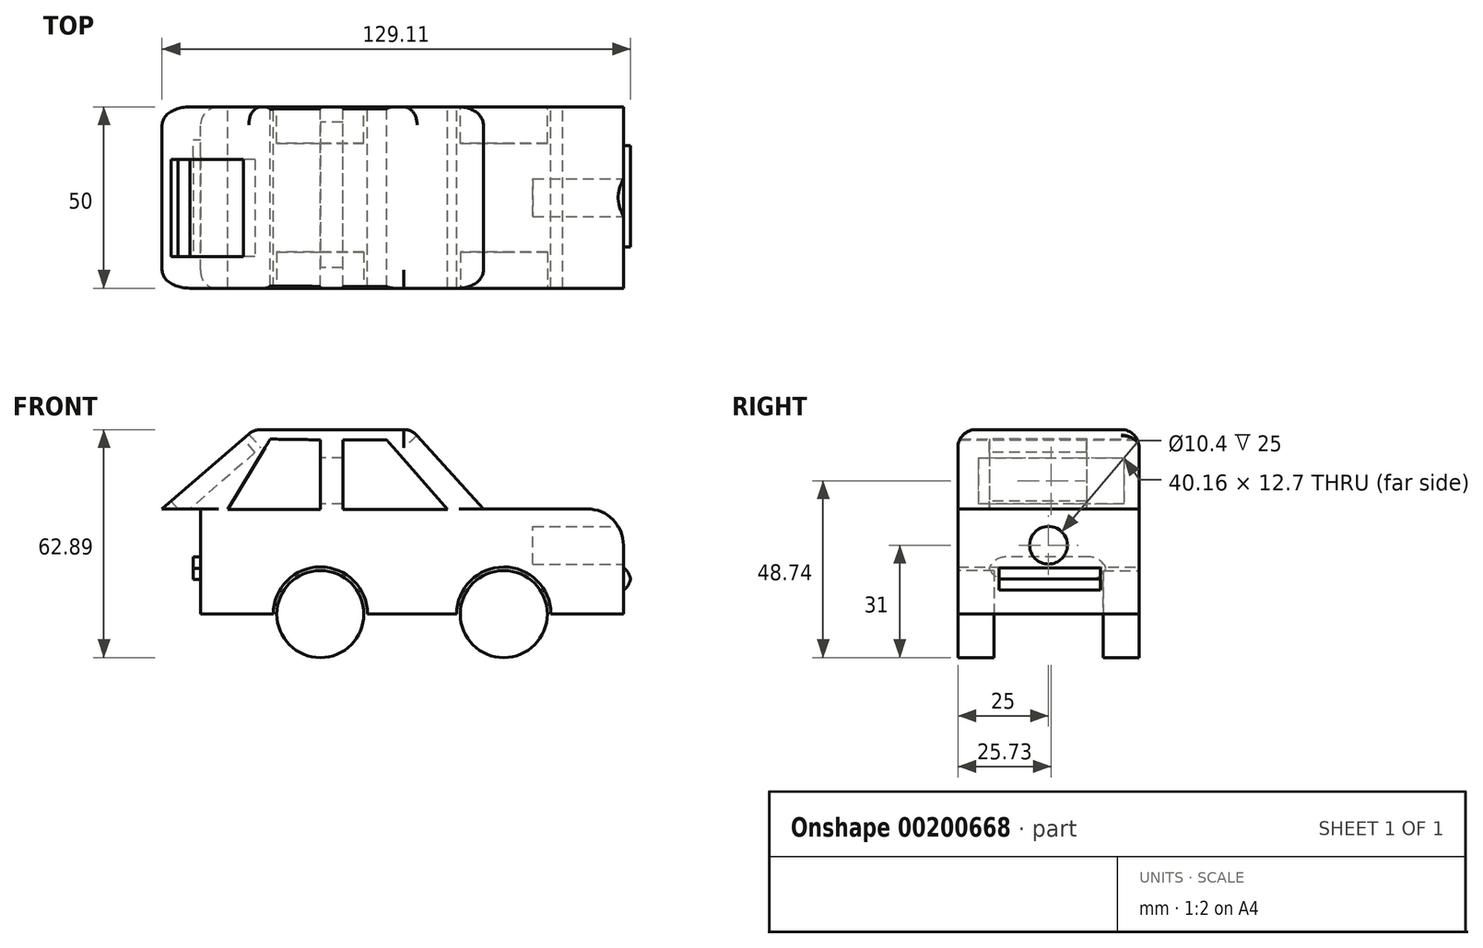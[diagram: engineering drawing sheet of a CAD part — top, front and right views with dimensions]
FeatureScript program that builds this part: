
annotation { "Feature Type Name" : "Feature", "Feature Type Description" : "" }
export const myFeature = defineFeature(function(context is Context, id is Id, definition is map)
    precondition{}
    {
        {
            var Q0;
            Q0=qCreatedBy(makeId("Front.planeOp"),FACE);
            var sketch = newSketch(context, id + "F0", { "sketchPlane" : qUnion([Q0])});
            skLineSegment(sketch, "E0", {"start": v(-31.77, -12.79) * mm, "end": v(-13, -12.79) * mm});
            skLineSegment(sketch, "E1", {"start": v(13, -12.79) * mm, "end": v(37.3, -12.79) * mm});
            skLineSegment(sketch, "E2", {"start": v(66.84, -12.79) * mm, "end": v(83.56, -12.79) * mm});
            skLineSegment(sketch, "E3", {"start": v(83.56, -12.79) * mm, "end": v(83.56, 16.21) * mm});
            skLineSegment(sketch, "E4", {"start": v(83.56, 16.21) * mm, "end": v(44.95, 16.21) * mm});
            skLineSegment(sketch, "E5", {"start": v(44.95, 16.21) * mm, "end": v(25.18, 38.1) * mm});
            skLineSegment(sketch, "E6", {"start": v(25.18, 38.1) * mm, "end": v(-18.32, 38.1) * mm});
            skLineSegment(sketch, "E7", {"start": v(-18.32, 38.1) * mm, "end": v(-43.63, 16.21) * mm});
            skLineSegment(sketch, "E8", {"start": v(-33, 16.21) * mm, "end": v(-43.63, 16.21) * mm});
            skLineSegment(sketch, "E9", {"start": v(-33, 16.21) * mm, "end": v(-33, -10.15) * mm});
            skLineSegment(sketch, "E10", {"start": v(-33, -10.15) * mm, "end": v(-33, -12.79) * mm});
            skLineSegment(sketch, "E11", {"start": v(-33, -12.79) * mm, "end": v(-31.77, -12.79) * mm});
            skArc(sketch, "E12", {"start": v(13, -12.79) * mm, "mid": v(0, 0.21) * mm, "end": v(-13, -12.79) * mm});
            skArc(sketch, "E13", {"start": v(63.56, -12.7) * mm, "mid": v(50.52, 0.21) * mm, "end": v(37.56, -12.79) * mm});
            skPoint(sketch, "E13.centerSnap0", {"position": v(7.3, -12.79) * mm});
            skLineSegment(sketch, "E14", {"start": v(63.56, -12.7) * mm, "end": v(66.84, -12.79) * mm});
            skLineSegment(sketch, "E15", {"start": v(37.3, -12.79) * mm, "end": v(37.56, -12.79) * mm});
            skPoint(sketch, "E16.trimOffspring.end.orphan", {"position": v(-22.7, -12.79) * mm});
            skSolve(sketch);
        }
        {
            var Q0;
            Q0=makeQuery(id+"F0.imprint","IMPRINT",FACE,{"disambiguationData":[TD([[makeQuery(id+"F0.imprint","IMPRINT",EDGE,{"derivedFrom":sQuery(id+"F0.wireOp",EDGE,"E0")}),1.0]])]});
            extrude(context, id + "F1", {"entities" : qUnion([Q0]), "endBound" : BoundingType.SYMMETRIC, "depth" : 50 * mm});
        }
        {
            var Q0;
            Q0=makeQuery(id+"F1.opExtrude","CAP_FACE",FACE,{"disambiguationData":[OSD([sQuery(id+"F0.wireOp",EDGE,"E0"),sQuery(id+"F0.wireOp",EDGE,"E1"),sQuery(id+"F0.wireOp",EDGE,"E2"),sQuery(id+"F0.wireOp",EDGE,"E3"),sQuery(id+"F0.wireOp",EDGE,"E4"),sQuery(id+"F0.wireOp",EDGE,"E5"),sQuery(id+"F0.wireOp",EDGE,"E6"),sQuery(id+"F0.wireOp",EDGE,"E7"),sQuery(id+"F0.wireOp",EDGE,"E8"),sQuery(id+"F0.wireOp",EDGE,"E9"),sQuery(id+"F0.wireOp",EDGE,"E10"),sQuery(id+"F0.wireOp",EDGE,"E11"),sQuery(id+"F0.wireOp",EDGE,"E12"),sQuery(id+"F0.wireOp",EDGE,"E13"),sQuery(id+"F0.wireOp",EDGE,"E14"),sQuery(id+"F0.wireOp",EDGE,"E15")])],"isStart":true});
            cPlane(context, id + "F2", {"entities" : qUnion([Q0]), "cplaneType" : CPlaneType.OFFSET, "offset" : 0 * mm, "oppositeDirection" : true, "width" : 150 * mm, "height" : 150 * mm});
        }
        {
            var Q0;
            Q0=makeQuery(id+"F1.opExtrude","CAP_FACE",FACE,{"disambiguationData":[OSD([sQuery(id+"F0.wireOp",EDGE,"E0"),sQuery(id+"F0.wireOp",EDGE,"E1"),sQuery(id+"F0.wireOp",EDGE,"E2"),sQuery(id+"F0.wireOp",EDGE,"E3"),sQuery(id+"F0.wireOp",EDGE,"E4"),sQuery(id+"F0.wireOp",EDGE,"E5"),sQuery(id+"F0.wireOp",EDGE,"E6"),sQuery(id+"F0.wireOp",EDGE,"E7"),sQuery(id+"F0.wireOp",EDGE,"E8"),sQuery(id+"F0.wireOp",EDGE,"E9"),sQuery(id+"F0.wireOp",EDGE,"E10"),sQuery(id+"F0.wireOp",EDGE,"E11"),sQuery(id+"F0.wireOp",EDGE,"E12"),sQuery(id+"F0.wireOp",EDGE,"E13"),sQuery(id+"F0.wireOp",EDGE,"E14"),sQuery(id+"F0.wireOp",EDGE,"E15")])],"isStart":true});
            var sketch = newSketch(context, id + "F3", { "sketchPlane" : qUnion([Q0])});
            skSolve(sketch);
        }
        {
            var Q0;
            Q0=qCreatedBy(id+"F2.planeOp",FACE);
            var sketch = newSketch(context, id + "F4", { "sketchPlane" : qUnion([Q0])});
            skPoint(sketch, "E17.0", {"position": v(-66.84, -12.79) * mm});
            skLineSegment(sketch, "E18.0", {"start": v(-66.84, -12.79) * mm, "end": v(-83.56, -12.79) * mm});
            skPoint(sketch, "E19.0", {"position": v(-63.56, -12.7) * mm});
            skPoint(sketch, "E20.0", {"position": v(-65.2, -12.74) * mm});
            skLineSegment(sketch, "E21.0", {"start": v(-13, -12.79) * mm, "end": v(-37.3, -12.79) * mm});
            skArc(sketch, "E22.0", {"start": v(-63.56, -12.7) * mm, "mid": v(-50.52, 0.21) * mm, "end": v(-37.56, -12.79) * mm});
            skCircle(sketch, "E23", {"center": v(-50.56, -12.79) * mm, "radius": 12 * mm});
            skCircle(sketch, "E24", {"center": v(0, -12.79) * mm, "radius": 12 * mm});
            skSolve(sketch);
        }
        {
            var Q0;
            Q0 = qSketchRegion(id + "F4", true);
            extrude(context, id + "F5", {"entities" : qUnion([Q0]), "oppositeDirection" : true, "depth" : 10 * mm});
        }
        {
            var Q0;
            Q0=makeQuery(id+"F5.opExtrude","SWEPT_BODY",BODY,{"disambiguationData":[OSD([sQuery(id+"F4.wireOp",EDGE,"E23")])]});
            var Q1;
            Q1=makeQuery(id+"F5.opExtrude","SWEPT_BODY",BODY,{"disambiguationData":[OSD([sQuery(id+"F4.wireOp",EDGE,"E24")])]});
            var Q2;
            Q2=qCreatedBy(makeId("Front.planeOp"),FACE);
            mirror(context, id + "F6", {"entities" : qUnion([Q0, Q1]), "mirrorPlane" : qUnion([Q2])});
        }
        {
            var Q0;
            Q0=makeQuery(id+"F3.imprint","IMPRINT",FACE,{"disambiguationData":[TD([[makeQuery(id+"F3.imprint","IMPRINT",EDGE,{"derivedFrom":makeQuery(id+"F1.opExtrude","CAP_EDGE",EDGE,{"disambiguationData":[OSD([sQuery(id+"F0.wireOp",EDGE,"E1")])],"isStart":true})}),-1.0]])]});
            var sketch = newSketch(context, id + "F7", { "sketchPlane" : qUnion([Q0])});
            skLineSegment(sketch, "E25", {"start": v(-35.1, 16.13) * mm, "end": v(-6.19, 16.13) * mm});
            skLineSegment(sketch, "E26", {"start": v(-6.19, 16.13) * mm, "end": v(-6.19, 32.53) * mm});
            skLineSegment(sketch, "E27", {"start": v(-6.19, 32.53) * mm, "end": v(-6.19, 35.27) * mm});
            skLineSegment(sketch, "E28", {"start": v(-6.19, 35.27) * mm, "end": v(-18.26, 35.27) * mm});
            skLineSegment(sketch, "E29", {"start": v(0, 35.27) * mm, "end": v(0, 16.13) * mm});
            skLineSegment(sketch, "E30", {"start": v(0, 16.13) * mm, "end": v(25.57, 16.13) * mm});
            skLineSegment(sketch, "E31", {"start": v(25.57, 16.13) * mm, "end": v(13.8, 35.48) * mm});
            skLineSegment(sketch, "E32", {"start": v(13.8, 35.48) * mm, "end": v(0, 35.27) * mm});
            skLineSegment(sketch, "E33", {"start": v(-35.1, 16.13) * mm, "end": v(-18.26, 35.27) * mm});
            skPoint(sketch, "E34.orphan", {"position": v(-23.65, 35.27) * mm});
            skSolve(sketch);
        }
        {
            var Q0;
            Q0=makeQuery(id+"F7.imprint","IMPRINT",FACE,{"disambiguationData":[TD([[makeQuery(id+"F7.imprint","IMPRINT",EDGE,{"derivedFrom":sQuery(id+"F7.wireOp",EDGE,"E25")}),1.0]])]});
            var Q1;
            Q1=makeQuery(id+"F7.imprint","IMPRINT",FACE,{"disambiguationData":[TD([[makeQuery(id+"F7.imprint","IMPRINT",EDGE,{"derivedFrom":sQuery(id+"F7.wireOp",EDGE,"E29")}),1.0]])]});
            extrude(context, id + "F8", {"entities" : qUnion([Q0, Q1]), "operationType" : NewBodyOperationType.REMOVE, "oppositeDirection" : true, "depth" : 100 * mm});
        }
        {
            var Q0;
            Q0=makeQuery(id+"F1.opExtrude","SWEPT_EDGE",EDGE,{"disambiguationData":[OSD([sQuery(id+"F0.wireOp",EDGE,"E3"),sQuery(id+"F0.wireOp",EDGE,"E4")])]});
            fillet(context, id + "F9", {"entities" : qUnion([Q0]), "radius" : 10 * mm, "tangentPropagation" : true, "allowEdgeOverflow" : false});
        }
        {
            var Q0;
            Q0=makeQuery(id+"F1.opExtrude","SWEPT_FACE",FACE,{"disambiguationData":[OSD([sQuery(id+"F0.wireOp",EDGE,"E3")])]});
            var sketch = newSketch(context, id + "F10", { "sketchPlane" : qUnion([Q0])});
            skCircle(sketch, "E35", {"center": v(0, 6.21) * mm, "radius": 5.2 * mm});
            skLineSegment(sketch, "E36", {"start": v(0, 6.21) * mm, "end": v(3.22, 2.14) * mm});
            skLineSegment(sketch, "E37", {"start": v(0, 6.21) * mm, "end": v(-2.15, 1.49) * mm});
            skLineSegment(sketch, "E38", {"start": v(-2.15, 1.49) * mm, "end": v(-3.04, 10.42) * mm});
            skLineSegment(sketch, "E39", {"start": v(3.22, 2.14) * mm, "end": v(3.22, 10.29) * mm});
            skSolve(sketch);
        }
        {
            var Q0;
            {var subQ0=sQuery(id+"F10.wireOp",EDGE,"E36");Q0=makeQuery(id+"F10.imprint","IMPRINT",FACE,{"disambiguationData":[TD([[makeQuery(id+"F10.imprint","IMPRINT",EDGE,{"derivedFrom":subQ0}),-1.0]])]});}
            var Q1;
            {var subQ0=sQuery(id+"F10.wireOp",EDGE,"E39");var subQ1=sQuery(id+"F10.wireOp",EDGE,"E35");var subQ2=makeQuery(id+"F10.imprint","INTERSECT",VERTEX,{"derivedFrom":[subQ1,subQ0]});Q1=makeQuery(id+"F10.imprint","IMPRINT",FACE,{"disambiguationData":[TD([[makeQuery(id+"F10.imprint","IMPRINT",EDGE,{"disambiguationData":[TD([[subQ2,1.0]])],"derivedFrom":subQ1}),1.0]])]});}
            var Q2;
            {var subQ0=sQuery(id+"F10.wireOp",EDGE,"E38");var subQ1=sQuery(id+"F10.wireOp",EDGE,"E35");var subQ2=makeQuery(id+"F10.imprint","INTERSECT",VERTEX,{"derivedFrom":[subQ1,subQ0]});Q2=makeQuery(id+"F10.imprint","IMPRINT",FACE,{"disambiguationData":[TD([[makeQuery(id+"F10.imprint","IMPRINT",EDGE,{"disambiguationData":[TD([[subQ2,-1.0]])],"derivedFrom":subQ1}),1.0]])]});}
            var Q3;
            {var subQ0=sQuery(id+"F10.wireOp",EDGE,"E38");var subQ1=sQuery(id+"F10.wireOp",EDGE,"E35");var subQ2=makeQuery(id+"F10.imprint","INTERSECT",VERTEX,{"derivedFrom":[subQ1,sQuery(id+"F10.wireOp",EDGE,"E37"),subQ0]});Q3=makeQuery(id+"F10.imprint","IMPRINT",FACE,{"disambiguationData":[TD([[makeQuery(id+"F10.imprint","IMPRINT",EDGE,{"disambiguationData":[TD([[subQ2,1.0]])],"derivedFrom":subQ1}),1.0]])]});}
            var Q4;
            {var subQ0=sQuery(id+"F10.wireOp",EDGE,"E39");var subQ1=sQuery(id+"F10.wireOp",EDGE,"E35");Q4=makeQuery(id+"F10.imprint","IMPRINT",FACE,{"disambiguationData":[TD([[makeQuery(id+"F10.imprint","IMPRINT",EDGE,{"disambiguationData":[TD([[makeQuery(id+"F10.imprint","INTERSECT",VERTEX,{"derivedFrom":[subQ1,sQuery(id+"F10.wireOp",EDGE,"E36"),subQ0]}),-1.0]])],"derivedFrom":subQ0}),-1.0]])]});}
            var Q5;
            {var subQ0=sQuery(id+"F10.wireOp",EDGE,"E37");Q5=makeQuery(id+"F10.imprint","IMPRINT",FACE,{"disambiguationData":[TD([[makeQuery(id+"F10.imprint","IMPRINT",EDGE,{"derivedFrom":subQ0}),-1.0]])]});}
            var Q6;
            {var subQ1=sQuery(id+"F10.wireOp",EDGE,"E35");var subQ6=sQuery(id+"F10.wireOp",EDGE,"E38");var subQ7=makeQuery(id+"F10.imprint","INTERSECT",VERTEX,{"derivedFrom":[subQ1,subQ6]});Q6=makeQuery(id+"F10.imprint","IMPRINT",FACE,{"disambiguationData":[TD([[makeQuery(id+"F10.imprint","IMPRINT",EDGE,{"disambiguationData":[TD([[subQ7,1.0]])],"derivedFrom":subQ1}),1.0]])]});}
            extrude(context, id + "F11", {"entities" : qUnion([Q0, Q1, Q2, Q3, Q4, Q5, Q6]), "operationType" : NewBodyOperationType.REMOVE, "oppositeDirection" : true, "depth" : 5 * mm});
        }
        {
            var Q0;
            {var subQ0=sQuery(id+"F10.wireOp",EDGE,"E38");var subQ1=sQuery(id+"F10.wireOp",EDGE,"E35");var subQ2=makeQuery(id+"F10.imprint","INTERSECT",VERTEX,{"derivedFrom":[subQ1,subQ0]});var subQ9=sQuery(id+"F10.wireOp",EDGE,"E37");var subQ10=sQuery(id+"F10.wireOp",EDGE,"E36");var subQ13=sQuery(id+"F10.wireOp",EDGE,"E39");var subQ14=makeQuery(id+"F10.imprint","INTERSECT",VERTEX,{"derivedFrom":[subQ1,subQ13]});var subQ18=makeQuery(id+"F10.imprint","IMPRINT",EDGE,{"derivedFrom":subQ10});var subQ19=makeQuery(id+"F10.imprint","INTERSECT",VERTEX,{"derivedFrom":[subQ1,subQ10,subQ13]});var subQ23=makeQuery(id+"F10.imprint","INTERSECT",VERTEX,{"derivedFrom":[subQ1,subQ9,subQ0]});var subQ24=makeQuery(id+"F10.imprint","IMPRINT",EDGE,{"derivedFrom":subQ9});Q0=qUnion([makeQuery(id+"F10.imprint","IMPRINT",FACE,{"disambiguationData":[TD([[makeQuery(id+"F10.imprint","IMPRINT",EDGE,{"disambiguationData":[TD([[subQ23,1.0]])],"derivedFrom":subQ1}),1.0]])]}),makeQuery(id+"F10.imprint","IMPRINT",FACE,{"disambiguationData":[TD([[subQ24,-1.0]])]}),makeQuery(id+"F10.imprint","IMPRINT",FACE,{"disambiguationData":[TD([[subQ18,-1.0]])]}),makeQuery(id+"F10.imprint","IMPRINT",FACE,{"disambiguationData":[TD([[makeQuery(id+"F10.imprint","IMPRINT",EDGE,{"disambiguationData":[TD([[subQ19,-1.0]])],"derivedFrom":subQ1}),1.0]])]}),makeQuery(id+"F10.imprint","IMPRINT",FACE,{"disambiguationData":[TD([[makeQuery(id+"F10.imprint","IMPRINT",EDGE,{"disambiguationData":[TD([[subQ14,1.0]])],"derivedFrom":subQ1}),1.0]])]}),makeQuery(id+"F10.imprint","IMPRINT",FACE,{"disambiguationData":[TD([[subQ18,1.0]])]}),makeQuery(id+"F10.imprint","IMPRINT",FACE,{"disambiguationData":[TD([[makeQuery(id+"F10.imprint","IMPRINT",EDGE,{"disambiguationData":[TD([[subQ2,1.0]])],"derivedFrom":subQ1}),1.0]])]}),makeQuery(id+"F10.imprint","IMPRINT",FACE,{"disambiguationData":[TD([[makeQuery(id+"F10.imprint","IMPRINT",EDGE,{"disambiguationData":[TD([[subQ2,-1.0]])],"derivedFrom":subQ1}),1.0]])]})]);}
            extrude(context, id + "F12", {"entities" : qUnion([Q0]), "operationType" : NewBodyOperationType.REMOVE, "oppositeDirection" : true, "depth" : 25 * mm});
        }
        {
            var Q0;
            Q0=makeQuery(id+"F1.opExtrude","SWEPT_FACE",FACE,{"disambiguationData":[OSD([sQuery(id+"F0.wireOp",EDGE,"E9"),sQuery(id+"F0.wireOp",EDGE,"E10")])]});
            var sketch = newSketch(context, id + "F13", { "sketchPlane" : qUnion([Q0])});
            skLineSegment(sketch, "E40.bottom", {"start": v(-16.24, 2.95) * mm, "end": v(16.78, 2.95) * mm});
            skLineSegment(sketch, "E40.top", {"start": v(-16.24, -3.22) * mm, "end": v(16.78, -3.22) * mm});
            skLineSegment(sketch, "E40.left", {"start": v(-16.24, 2.95) * mm, "end": v(-16.24, -3.22) * mm});
            skLineSegment(sketch, "E40.right", {"start": v(16.78, 2.95) * mm, "end": v(16.78, -3.22) * mm});
            skSolve(sketch);
        }
        {
            var Q0;
            Q0=makeQuery(id+"F13.imprint","IMPRINT",FACE,{"disambiguationData":[TD([[makeQuery(id+"F13.imprint","IMPRINT",EDGE,{"derivedFrom":sQuery(id+"F13.wireOp",EDGE,"E40.bottom")}),-1.0]])]});
            extrude(context, id + "F14", {"entities" : qUnion([Q0]), "operationType" : NewBodyOperationType.ADD, "depth" : 2 * mm});
        }
        {
            var Q0;
            Q0=makeQuery(id+"F1.opExtrude","SWEPT_FACE",FACE,{"disambiguationData":[OSD([sQuery(id+"F0.wireOp",EDGE,"E3")])]});
            var sketch = newSketch(context, id + "F15", { "sketchPlane" : qUnion([Q0])});
            skLineSegment(sketch, "E41.bottom", {"start": v(-13.6, -6.2) * mm, "end": v(14.33, -6.2) * mm});
            skLineSegment(sketch, "E41.top", {"start": v(-13.6, 0) * mm, "end": v(14.33, 0) * mm});
            skLineSegment(sketch, "E41.left", {"start": v(-13.6, -6.2) * mm, "end": v(-13.6, 0) * mm});
            skLineSegment(sketch, "E41.right", {"start": v(14.33, -6.2) * mm, "end": v(14.33, 0) * mm});
            skSolve(sketch);
        }
        {
            var Q0;
            Q0=makeQuery(id+"F15.imprint","IMPRINT",FACE,{"disambiguationData":[TD([[makeQuery(id+"F15.imprint","IMPRINT",EDGE,{"derivedFrom":sQuery(id+"F15.wireOp",EDGE,"E41.bottom")}),1.0]])]});
            extrude(context, id + "F16", {"entities" : qUnion([Q0]), "operationType" : NewBodyOperationType.ADD, "depth" : 2 * mm});
        }
        {
            var Q0;
            Q0=makeQuery(id+"F16.opExtrude","CAP_EDGE",EDGE,{"disambiguationData":[OSD([sQuery(id+"F15.wireOp",EDGE,"E41.top")])],"isStart":false});
            var Q1;
            Q1=makeQuery(id+"F16.opExtrude","CAP_EDGE",EDGE,{"disambiguationData":[OSD([sQuery(id+"F15.wireOp",EDGE,"E41.bottom")])],"isStart":false});
            fillet(context, id + "F17", {"entities" : qUnion([Q0, Q1]), "radius" : 5 * mm, "tangentPropagation" : true, "allowEdgeOverflow" : false});
        }
        {
            var Q0;
            Q0=makeQuery(id+"F14.opExtrude","SWEPT_EDGE",EDGE,{"disambiguationData":[OSD([sQuery(id+"F13.wireOp",EDGE,"E40.bottom"),sQuery(id+"F13.wireOp",EDGE,"E40.left")])]});
            var Q1;
            Q1=makeQuery(id+"F14.opExtrude","SWEPT_EDGE",EDGE,{"disambiguationData":[OSD([sQuery(id+"F13.wireOp",EDGE,"E40.bottom"),sQuery(id+"F13.wireOp",EDGE,"E40.right")])]});
            var Q2;
            Q2=makeQuery(id+"F14.opExtrude","SWEPT_EDGE",EDGE,{"disambiguationData":[OSD([sQuery(id+"F13.wireOp",EDGE,"E40.top"),sQuery(id+"F13.wireOp",EDGE,"E40.left")])]});
            var Q3;
            Q3=makeQuery(id+"F14.opExtrude","SWEPT_EDGE",EDGE,{"disambiguationData":[OSD([sQuery(id+"F13.wireOp",EDGE,"E40.top"),sQuery(id+"F13.wireOp",EDGE,"E40.right")])]});
            fillet(context, id + "F18", {"entities" : qUnion([Q0, Q1, Q2, Q3]), "radius" : 5 * mm, "tangentPropagation" : true, "allowEdgeOverflow" : false});
        }
        {
            var Q0;
            Q0=makeQuery(id+"F1.opExtrude","SWEPT_FACE",FACE,{"disambiguationData":[OSD([sQuery(id+"F0.wireOp",EDGE,"E7")])]});
            var sketch = newSketch(context, id + "F19", { "sketchPlane" : qUnion([Q0])});
            skLineSegment(sketch, "E42.bottom", {"start": v(7.2, 10.52) * mm, "end": v(-19.03, 10.52) * mm});
            skLineSegment(sketch, "E42.top", {"start": v(7.2, -16.32) * mm, "end": v(-19.03, -16.32) * mm});
            skLineSegment(sketch, "E42.left", {"start": v(7.2, 10.52) * mm, "end": v(7.2, -16.32) * mm});
            skLineSegment(sketch, "E42.right", {"start": v(-19.03, 10.52) * mm, "end": v(-19.03, -16.32) * mm});
            skSolve(sketch);
        }
        {
            var Q0;
            Q0 = qSketchRegion(id + "F19", true);
            extrude(context, id + "F20", {"entities" : qUnion([Q0]), "operationType" : NewBodyOperationType.REMOVE, "oppositeDirection" : true, "depth" : 5 * mm});
        }
        {
            var Q0;
            Q0=qCreatedBy(makeId("Right.planeOp"),FACE);
            var sketch = newSketch(context, id + "F21", { "sketchPlane" : qUnion([Q0])});
            skLineSegment(sketch, "E43", {"start": v(20.81, 30.3) * mm, "end": v(20.81, 17.6) * mm});
            skLineSegment(sketch, "E44", {"start": v(20.81, 17.6) * mm, "end": v(-19.35, 17.6) * mm});
            skLineSegment(sketch, "E45", {"start": v(-19.35, 30.3) * mm, "end": v(20.81, 30.3) * mm});
            skLineSegment(sketch, "E46", {"start": v(-19.35, 30.3) * mm, "end": v(-19.35, 17.6) * mm});
            skPoint(sketch, "E47.orphan", {"position": v(-25.19, 30.3) * mm});
            skSolve(sketch);
        }
        {
            var Q0;
            Q0 = qSketchRegion(id + "F21", true);
            extrude(context, id + "F22", {"entities" : qUnion([Q0]), "operationType" : NewBodyOperationType.REMOVE, "depth" : 20 * mm});
        }
        {
            var Q0;
            Q0 = qSketchRegion(id + "F21", true);
            extrude(context, id + "F23", {"entities" : qUnion([Q0]), "operationType" : NewBodyOperationType.REMOVE, "depth" : 20 * mm});
        }
        {
            var Q0;
            Q0=makeQuery(id+"F1.opExtrude","SWEPT_EDGE",EDGE,{"disambiguationData":[OSD([sQuery(id+"F0.wireOp",EDGE,"E6"),sQuery(id+"F0.wireOp",EDGE,"E7")])]});
            var Q1;
            Q1=makeQuery(id+"F1.opExtrude","CAP_EDGE",EDGE,{"disambiguationData":[OSD([sQuery(id+"F0.wireOp",EDGE,"E7")])],"isStart":true});
            fillet(context, id + "F24", {"entities" : qUnion([Q0, Q1]), "radius" : 5 * mm, "tangentPropagation" : true, "allowEdgeOverflow" : false});
        }
        {
            var Q0;
            Q0=makeQuery(id+"F1.opExtrude","CAP_EDGE",EDGE,{"disambiguationData":[OSD([sQuery(id+"F0.wireOp",EDGE,"E7")])],"isStart":false});
            var Q1;
            Q1=makeQuery(id+"F1.opExtrude","CAP_EDGE",EDGE,{"disambiguationData":[OSD([sQuery(id+"F0.wireOp",EDGE,"E6")])],"isStart":false});
            fillet(context, id + "F25", {"entities" : qUnion([Q0, Q1]), "radius" : 5 * mm, "tangentPropagation" : true, "allowEdgeOverflow" : false});
        }
        {
            var Q0;
            Q0=makeQuery(id+"F1.opExtrude","CAP_EDGE",EDGE,{"disambiguationData":[OSD([sQuery(id+"F0.wireOp",EDGE,"E5")])],"isStart":true});
            fillet(context, id + "F26", {"entities" : qUnion([Q0]), "radius" : 5 * mm, "allowEdgeOverflow" : false});
        }
        {
            var Q0;
            Q0=makeQuery(id+"F1.opExtrude","CAP_EDGE",EDGE,{"disambiguationData":[OSD([sQuery(id+"F0.wireOp",EDGE,"E5")])],"isStart":false});
            fillet(context, id + "F27", {"entities" : qUnion([Q0]), "radius" : 5 * mm, "tangentPropagation" : true, "allowEdgeOverflow" : false});
        }
        {
            var Q0;
            Q0=makeQuery(id+"F1.opExtrude","CAP_EDGE",EDGE,{"disambiguationData":[OSD([sQuery(id+"F0.wireOp",EDGE,"E9"),sQuery(id+"F0.wireOp",EDGE,"E10")])],"isStart":false});
            fillet(context, id + "F28", {"entities" : qUnion([Q0]), "radius" : 5 * mm, "rho" : 0.5, "crossSection" : FilletCrossSection.CONIC, "allowEdgeOverflow" : false});
        }
        {
            var Q0;
            Q0=makeQuery(id+"F1.opExtrude","CAP_EDGE",EDGE,{"disambiguationData":[OSD([sQuery(id+"F0.wireOp",EDGE,"E9"),sQuery(id+"F0.wireOp",EDGE,"E10")])],"isStart":true});
            fillet(context, id + "F29", {"entities" : qUnion([Q0]), "radius" : 5 * mm, "tangentPropagation" : true, "allowEdgeOverflow" : false});
        }
    });
